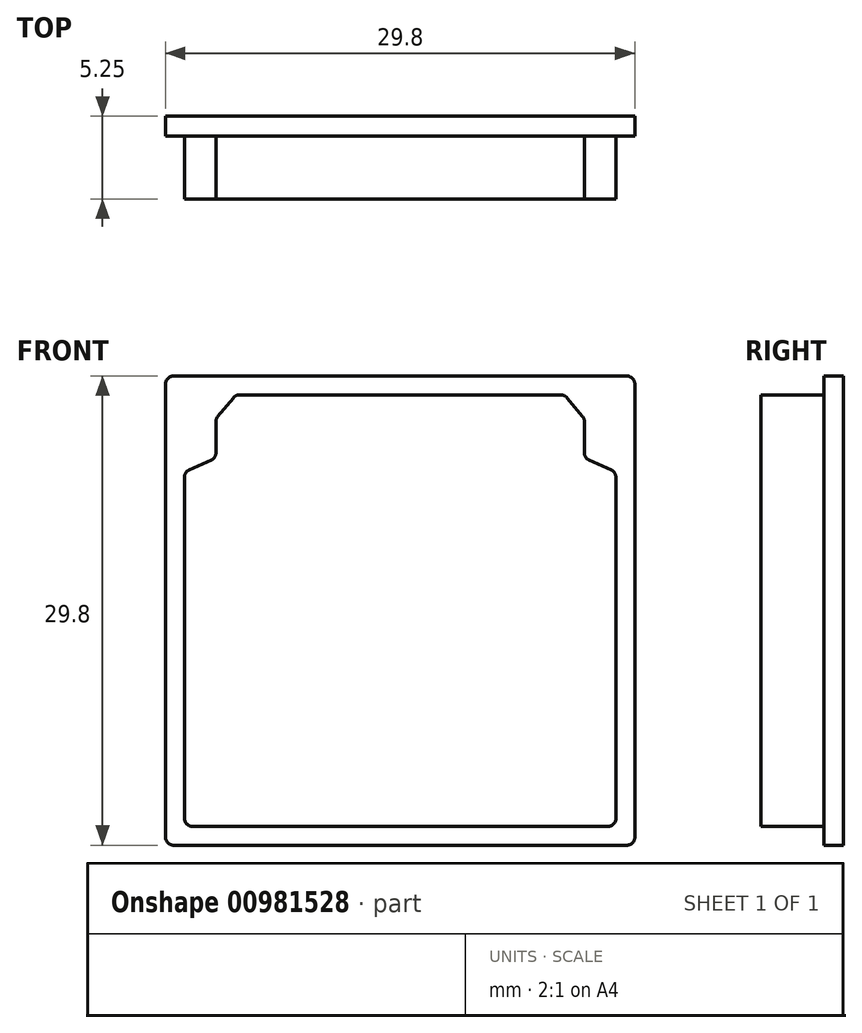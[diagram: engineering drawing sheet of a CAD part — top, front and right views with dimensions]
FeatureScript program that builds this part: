
annotation { "Feature Type Name" : "Feature", "Feature Type Description" : "" }
export const myFeature = defineFeature(function(context is Context, id is Id, definition is map)
    precondition{}
    {
        {
            var Q0;
            Q0=qCreatedBy(makeId("Front.planeOp"),FACE);
            var sketch = newSketch(context, id + "F0", { "sketchPlane" : qUnion([Q0])});
            skLineSegment(sketch, "E0.bottom", {"start": v(-14.9, 14.9) * mm, "end": v(14.9, 14.9) * mm});
            skLineSegment(sketch, "E0.top", {"start": v(-14.9, -14.9) * mm, "end": v(14.9, -14.9) * mm});
            skLineSegment(sketch, "E0.left", {"start": v(-14.9, 14.9) * mm, "end": v(-14.9, -14.9) * mm});
            skLineSegment(sketch, "E0.right", {"start": v(14.9, 14.9) * mm, "end": v(14.9, -14.9) * mm});
            skSolve(sketch);
        }
        {
            var Q0;
            Q0 = qSketchRegion(id + "F0", true);
            extrude(context, id + "F1", {"entities" : qUnion([Q0]), "depth" : 1.25 * mm, "offsetDistance" : 25 * mm});
        }
        {
            var Q0;
            Q0=makeQuery(id+"F1.opExtrude","CAP_FACE",FACE,{"disambiguationData":[OSD([sQuery(id+"F0.wireOp",EDGE,"E0.bottom"),sQuery(id+"F0.wireOp",EDGE,"E0.top"),sQuery(id+"F0.wireOp",EDGE,"E0.left"),sQuery(id+"F0.wireOp",EDGE,"E0.right")])],"isStart":false});
            var sketch = newSketch(context, id + "F2", { "sketchPlane" : qUnion([Q0])});
            skLineSegment(sketch, "E1", {"start": v(0, -13.7) * mm, "end": v(13.7, -13.7) * mm});
            skLineSegment(sketch, "E2", {"start": v(13.7, -13.7) * mm, "end": v(13.7, 8.8) * mm});
            skLineSegment(sketch, "E3", {"start": v(13.7, 8.8) * mm, "end": v(11.7, 9.7) * mm});
            skLineSegment(sketch, "E4", {"start": v(11.7, 9.7) * mm, "end": v(11.7, 12.2) * mm});
            skLineSegment(sketch, "E5", {"start": v(11.7, 12.2) * mm, "end": v(10.45, 13.7) * mm});
            skLineSegment(sketch, "E6", {"start": v(10.45, 13.7) * mm, "end": v(0, 13.7) * mm});
            skLineSegment(sketch, "E7", {"start": v(0, 14.9) * mm, "end": v(0, -14.9) * mm, "construction": true});
            skLineSegment(sketch, "E8.MirrorCS", {"start": v(-10.45, 13.7) * mm, "end": v(0, 13.7) * mm});
            skLineSegment(sketch, "E9.MirrorCS", {"start": v(-11.7, 12.2) * mm, "end": v(-10.45, 13.7) * mm});
            skLineSegment(sketch, "E10.MirrorCS", {"start": v(-11.7, 9.7) * mm, "end": v(-11.7, 12.2) * mm});
            skLineSegment(sketch, "E11.MirrorCS", {"start": v(-13.7, 8.8) * mm, "end": v(-11.7, 9.7) * mm});
            skLineSegment(sketch, "E12.MirrorCS", {"start": v(-13.7, -13.7) * mm, "end": v(-13.7, 8.8) * mm});
            skLineSegment(sketch, "E13.MirrorCS", {"start": v(0, -13.7) * mm, "end": v(-13.7, -13.7) * mm});
            skSolve(sketch);
        }
        {
            var Q0;
            Q0 = qSketchRegion(id + "F2", true);
            extrude(context, id + "F3", {"entities" : qUnion([Q0]), "operationType" : NewBodyOperationType.ADD, "depth" : 4 * mm, "offsetDistance" : 25 * mm});
        }
        {
            var Q0;
            Q0=makeQuery(id+"F1.opExtrude","SWEPT_EDGE",EDGE,{"disambiguationData":[OSD([sQuery(id+"F0.wireOp",EDGE,"E0.bottom"),sQuery(id+"F0.wireOp",EDGE,"E0.left")])]});
            var Q1;
            Q1=makeQuery(id+"F1.opExtrude","SWEPT_EDGE",EDGE,{"disambiguationData":[OSD([sQuery(id+"F0.wireOp",EDGE,"E0.top"),sQuery(id+"F0.wireOp",EDGE,"E0.left")])]});
            var Q2;
            Q2=makeQuery(id+"F3.opExtrude","SWEPT_EDGE",EDGE,{"disambiguationData":[OSD([sQuery(id+"F2.wireOp",EDGE,"E9.MirrorCS"),sQuery(id+"F2.wireOp",EDGE,"E10.MirrorCS")])]});
            var Q3;
            Q3=makeQuery(id+"F3.opExtrude","SWEPT_EDGE",EDGE,{"disambiguationData":[OSD([sQuery(id+"F2.wireOp",EDGE,"E8.MirrorCS"),sQuery(id+"F2.wireOp",EDGE,"E9.MirrorCS")])]});
            var Q4;
            Q4=makeQuery(id+"F3.opExtrude","SWEPT_EDGE",EDGE,{"disambiguationData":[OSD([sQuery(id+"F2.wireOp",EDGE,"E10.MirrorCS"),sQuery(id+"F2.wireOp",EDGE,"E11.MirrorCS")])]});
            var Q5;
            Q5=makeQuery(id+"F3.opExtrude","SWEPT_EDGE",EDGE,{"disambiguationData":[OSD([sQuery(id+"F2.wireOp",EDGE,"E11.MirrorCS"),sQuery(id+"F2.wireOp",EDGE,"E12.MirrorCS")])]});
            var Q6;
            Q6=makeQuery(id+"F3.opExtrude","SWEPT_EDGE",EDGE,{"disambiguationData":[OSD([sQuery(id+"F2.wireOp",EDGE,"E12.MirrorCS"),sQuery(id+"F2.wireOp",EDGE,"E13.MirrorCS")])]});
            var Q7;
            Q7=makeQuery(id+"F1.opExtrude","SWEPT_EDGE",EDGE,{"disambiguationData":[OSD([sQuery(id+"F0.wireOp",EDGE,"E0.bottom"),sQuery(id+"F0.wireOp",EDGE,"E0.right")])]});
            var Q8;
            Q8=makeQuery(id+"F1.opExtrude","SWEPT_EDGE",EDGE,{"disambiguationData":[OSD([sQuery(id+"F0.wireOp",EDGE,"E0.top"),sQuery(id+"F0.wireOp",EDGE,"E0.right")])]});
            var Q9;
            Q9=makeQuery(id+"F3.opExtrude","SWEPT_EDGE",EDGE,{"disambiguationData":[OSD([sQuery(id+"F2.wireOp",EDGE,"E1"),sQuery(id+"F2.wireOp",EDGE,"E2")])]});
            var Q10;
            Q10=makeQuery(id+"F3.opExtrude","SWEPT_EDGE",EDGE,{"disambiguationData":[OSD([sQuery(id+"F2.wireOp",EDGE,"E2"),sQuery(id+"F2.wireOp",EDGE,"E3")])]});
            var Q11;
            Q11=makeQuery(id+"F3.opExtrude","SWEPT_EDGE",EDGE,{"disambiguationData":[OSD([sQuery(id+"F2.wireOp",EDGE,"E3"),sQuery(id+"F2.wireOp",EDGE,"E4")])]});
            var Q12;
            Q12=makeQuery(id+"F3.opExtrude","SWEPT_EDGE",EDGE,{"disambiguationData":[OSD([sQuery(id+"F2.wireOp",EDGE,"E4"),sQuery(id+"F2.wireOp",EDGE,"E5")])]});
            var Q13;
            Q13=makeQuery(id+"F3.opExtrude","SWEPT_EDGE",EDGE,{"disambiguationData":[OSD([sQuery(id+"F2.wireOp",EDGE,"E5"),sQuery(id+"F2.wireOp",EDGE,"E6")])]});
            fillet(context, id + "F4", {"entities" : qUnion([Q0, Q1, Q2, Q3, Q4, Q5, Q6, Q7, Q8, Q9, Q10, Q11, Q12, Q13]), "radius" : 0.5 * mm, "tangentPropagation" : true, "allowEdgeOverflow" : false});
        }
    });
